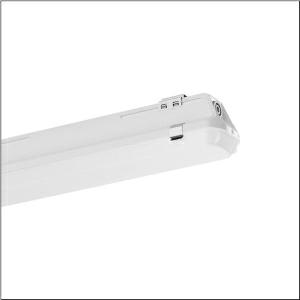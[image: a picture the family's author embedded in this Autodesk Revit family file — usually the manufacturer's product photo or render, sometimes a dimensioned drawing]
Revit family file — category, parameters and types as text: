
# Revit family: monsun_r__21_51fb10mp680b_ab58
name_source: partatom
category: Lighting Fixtures
units: mm (PartAtom-declared; Revit-internal decimal feet)

## family parameters
Cut with Voids When Loaded = No
Host = Face
Light Source = No
Part Type = Normal
Room Calculation Point = No
Round Connector Dimension = Use Diameter
Shared = No

## types (1)
- --- (1 x LED, 8190 lm, 53.6 W, 6500K)
    Apparent Load = 54 VA
    CIE Flux Codes = 47 77 93 94 100
    Color Rendering = 80
    Color Temperature = 6500K
    Default Elevation = 1800 mm
    Description = Monsun® 21, damp-proof luminaire, chain hanger, primary optical cover: enclosure, of PMMA, light emission: direct distribution, primary light characteristic: symmetric, installation type: suspended mounting, surface-mounted, horizontal mounting, vertical mounting, LED, rated luminous flux: 8.190lm, luminous efficacy: 153lm/W, light colour: 865, colour temperature: 6500K, control gear: ECG, with terminal, 3-pole, max. 2.5mm², mains connection: 220..240V, AC, 50/60Hz, rated input power: 54W, housing, of glass-fibre reinforced polyester, uncoated, bright grey, incl. chain hanger, length: 1.590mm, width: 90mm, height: 88mm, clip for enclosure, of stainless steel (V2A), ceiling mounting element, of stainless steel (V2A), chain hanger, of stainless steel (V2A), protection rating (complete): IP66, insulation class (complete): insulation class I (protective earthing), certification: CE, ENEC, VDE, UKCA, protection symbol: D, impact resistance: IK04, permissible operating ambient temperature: -25..+35°C, standard: EN 50419, EN 60598-2-1, corresponds to IFS (International Featured Standards) requirements for safety and quality in the food industry, for indoor or canopied outdoor use, no direct snow, no direct sun, no direct rain, contact your sales advisor before using the luminaires in applications with unclear chemical exposure, large temperature fluctuations or condensation-forming humidity, LABS conformity tested according to VDMA 24364:2018-05, packaging unit: 1 piece
    Height = 89 mm
    Lamp = 1 x LED
    Lamp Light Flux = 8190 lm
    Lamp Power = 53.6 W
    Lamp count = 1
    Length = 1590 mm
    Luminous efficacy = 153 lm/W
    Manufacturer = Siteco
    ModVariant = No
    Model = 51FB10MP680B
    Mounting Place = Ceiling
    Mounting Type = Surface mounted
    Number of Poles = 1
    OnlyDefault = Yes
    Power Factor = 1
    Product Name = Monsun® 21
    Product group = damp-proof luminaire
    ProductGroupID = 300
    Protection Class = Protection class I
    Protection Degree = IP 66
    RLX_Detail_Level = 1
    RLX_Emergency_Light_Flux = 0 lm
    RLX_Emergency_Type = 0
    RLX_Emergency_Type_DB = No
    RlxData = <blob elided: 89937 chars, md5=ff5242c8>
    Socket = socket
    Standby Power = 0 W
    System Light Flux = 8190 lm
    System Power = 54 W
    Type Comments = factory setting: luminous flux: 100 % | (A | C | E) | 121 mA
    Type Image = l_1319656.jpg
    URL = http://relux.com
    VarID = @adj_117143
    Voltage = 0 V
    Weight = 0.00 kg
    Width = 90 mm

## geometry (parser evidence)
native form markers: Blend x4, Sweep x14
no freeform markers — native parametric forms only
